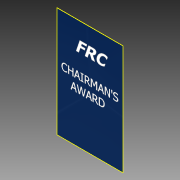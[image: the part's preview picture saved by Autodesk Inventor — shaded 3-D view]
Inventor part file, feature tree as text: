
AUTODESK INVENTOR PART (.ipt)
format: ipt  version: 2014 (Build 180170000, 170)  size: 81,408 bytes
history: native  units: in
note: dims shown in document units (in); Inventor stores cm internally (conversion verified against a paired STEP export)
features: sketch x2, extrude x1
ambient origin geometry x8: Origin, YZ Plane, XZ Plane, XY Plane, X Axis, Y Axis, Z Axis, Center Point
bodies: Solid1 (feature_tree)
feature tree (3):
  extrude  "Extrusion1"  Depth=60.0in
  sketch  "Sketch2"  dims[d2=0.2in d3=0.0in]
  sketch  "Sketch1"  dims[d0=36.0in d1=60.0in]
